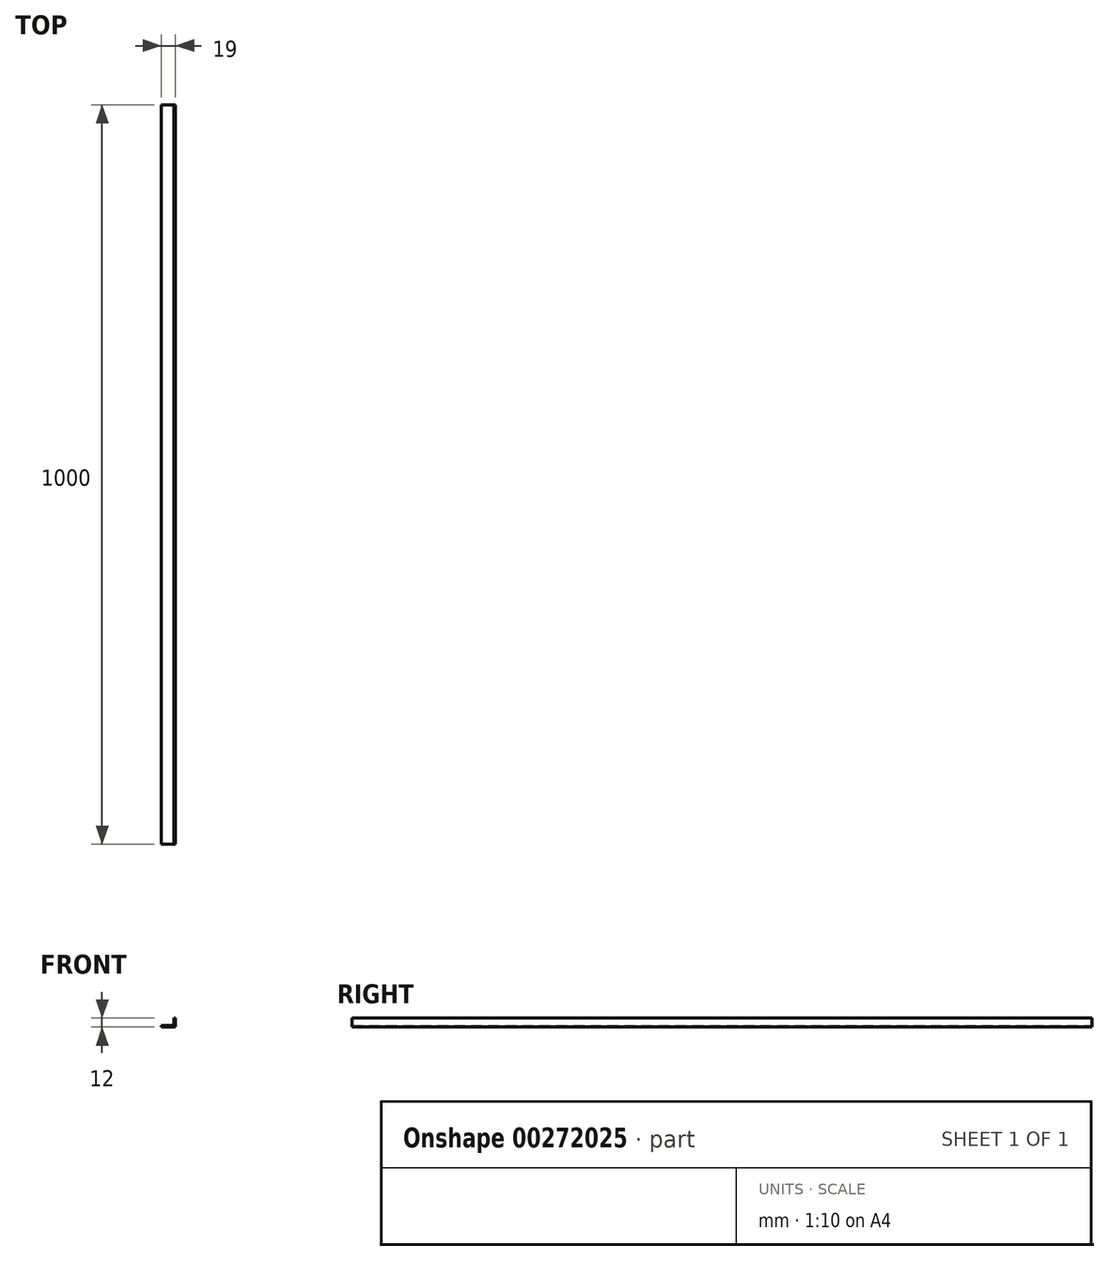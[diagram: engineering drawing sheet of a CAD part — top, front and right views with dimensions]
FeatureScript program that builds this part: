
annotation { "Feature Type Name" : "Feature", "Feature Type Description" : "" }
export const myFeature = defineFeature(function(context is Context, id is Id, definition is map)
    precondition{}
    {
        {
            var Q0;
            Q0=qCreatedBy(makeId("Front.planeOp"),FACE);
            var sketch = newSketch(context, id + "F0", { "sketchPlane" : qUnion([Q0])});
            skLineSegment(sketch, "E0", {"start": v(0, 0) * mm, "end": v(-19, 0) * mm});
            skLineSegment(sketch, "E1", {"start": v(-19, 0) * mm, "end": v(-19, 2) * mm});
            skLineSegment(sketch, "E2", {"start": v(-19, 2) * mm, "end": v(-2, 2) * mm});
            skLineSegment(sketch, "E3", {"start": v(-2, 2) * mm, "end": v(-2, 12) * mm});
            skLineSegment(sketch, "E4", {"start": v(-2, 12) * mm, "end": v(0, 12) * mm});
            skLineSegment(sketch, "E5", {"start": v(0, 12) * mm, "end": v(0, 0) * mm});
            skSolve(sketch);
        }
        {
            var Q0;
            Q0=makeQuery(id+"F0.imprint","IMPRINT",FACE,{"disambiguationData":[TD([[makeQuery(id+"F0.imprint","IMPRINT",EDGE,{"derivedFrom":sQuery(id+"F0.wireOp",EDGE,"E0")}),-1.0]])]});
            extrude(context, id + "F1", {"entities" : qUnion([Q0]), "endBound" : BoundingType.SYMMETRIC, "depth" : 1000 * mm});
        }
    });
